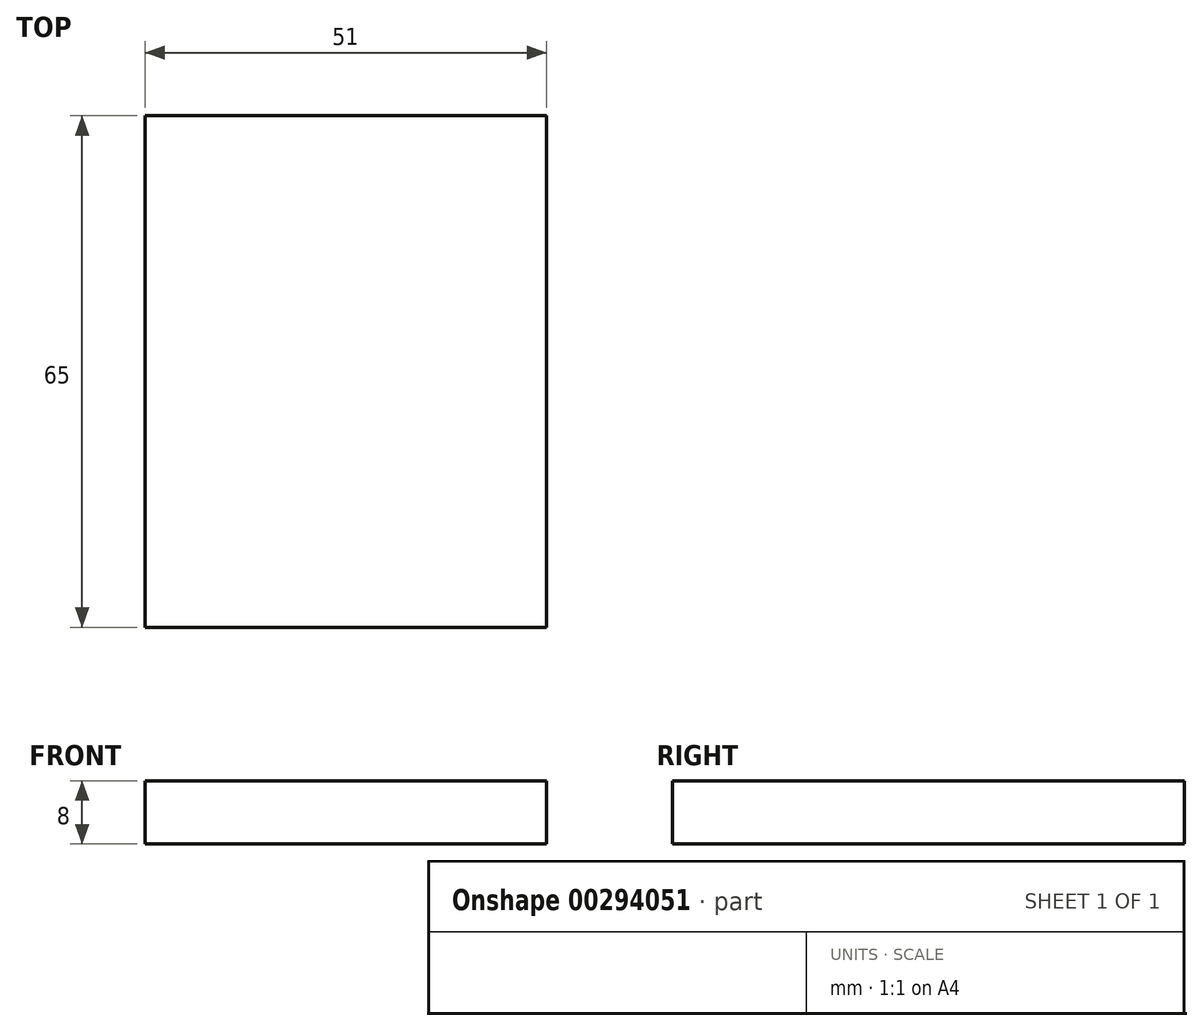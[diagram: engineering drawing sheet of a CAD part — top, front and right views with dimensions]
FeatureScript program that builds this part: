
annotation { "Feature Type Name" : "Feature", "Feature Type Description" : "" }
export const myFeature = defineFeature(function(context is Context, id is Id, definition is map)
    precondition{}
    {
        {
            var Q0;
            Q0=qCreatedBy(makeId("Top.planeOp"),FACE);
            var sketch = newSketch(context, id + "F0", { "sketchPlane" : qUnion([Q0])});
            skLineSegment(sketch, "E0.bottom", {"start": v(-25.5, 32.5) * mm, "end": v(25.5, 32.5) * mm});
            skLineSegment(sketch, "E0.top", {"start": v(-25.5, -32.5) * mm, "end": v(25.5, -32.5) * mm});
            skLineSegment(sketch, "E0.left", {"start": v(-25.5, 32.5) * mm, "end": v(-25.5, -32.5) * mm});
            skLineSegment(sketch, "E0.right", {"start": v(25.5, 32.5) * mm, "end": v(25.5, -32.5) * mm});
            skPoint(sketch, "E0.middle", {"position": v(0, 0) * mm});
            skSolve(sketch);
        }
        {
            var Q0;
            Q0 = qSketchRegion(id + "F0", true);
            extrude(context, id + "F1", {"entities" : qUnion([Q0]), "depth" : 8 * mm});
        }
    });
